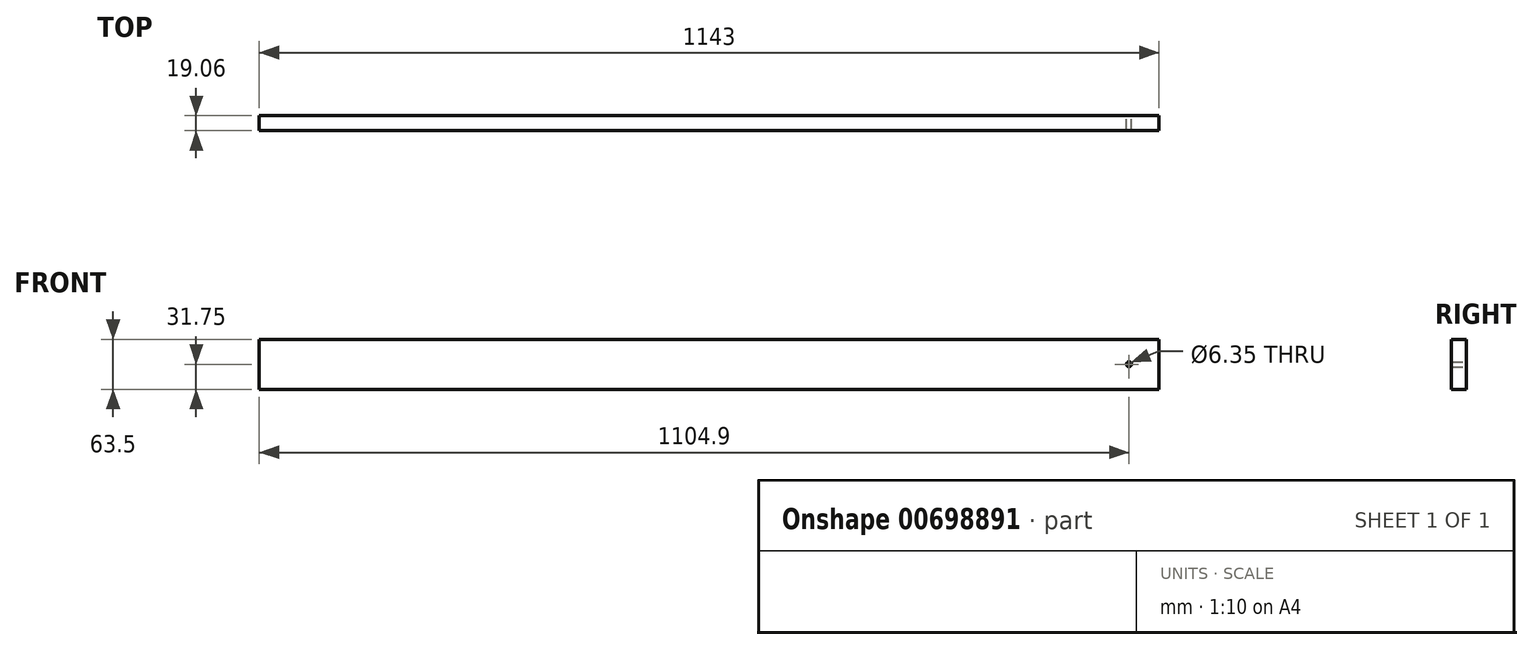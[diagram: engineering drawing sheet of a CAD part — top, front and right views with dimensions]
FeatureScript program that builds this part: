
annotation { "Feature Type Name" : "Feature", "Feature Type Description" : "" }
export const myFeature = defineFeature(function(context is Context, id is Id, definition is map)
    precondition{}
    {
        {
            var Q0;
            Q0=qCreatedBy(makeId("Front.planeOp"),FACE);
            var sketch = newSketch(context, id + "F0", { "sketchPlane" : qUnion([Q0])});
            skLineSegment(sketch, "E0.bottom", {"start": v(571.5, 31.75) * mm, "end": v(-571.5, 31.75) * mm});
            skLineSegment(sketch, "E0.top", {"start": v(571.5, -31.75) * mm, "end": v(-571.5, -31.75) * mm});
            skLineSegment(sketch, "E0.left", {"start": v(571.5, 31.75) * mm, "end": v(571.5, -31.75) * mm});
            skLineSegment(sketch, "E0.right", {"start": v(-571.5, 31.75) * mm, "end": v(-571.5, -31.75) * mm});
            skPoint(sketch, "E0.middle", {"position": v(0, 0) * mm});
            skCircle(sketch, "E1", {"center": v(533.4, 0) * mm, "radius": 3.18 * mm});
            skSolve(sketch);
        }
        {
            var Q0;
            Q0=qSketchRegion(id+"F0",true);
            extrude(context, id + "F1", {"entities" : qUnion([Q0]), "endBound" : BoundingType.SYMMETRIC, "depth" : 19.05 * mm, "offsetDistance" : 25.4 * mm});
        }
    });
